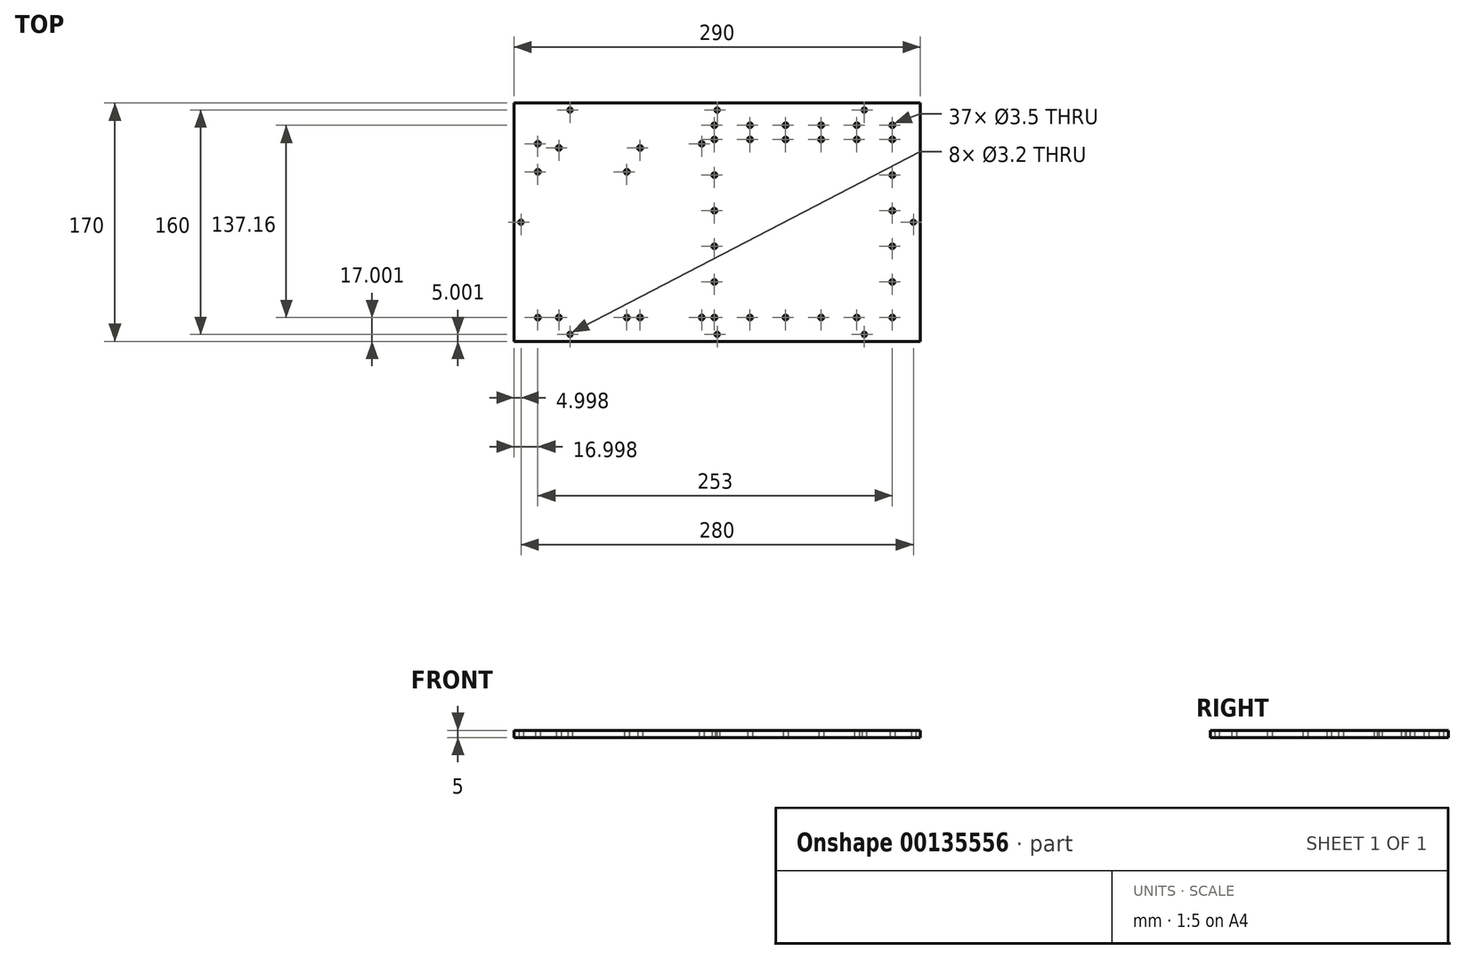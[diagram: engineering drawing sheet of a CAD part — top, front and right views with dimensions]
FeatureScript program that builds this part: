
annotation { "Feature Type Name" : "Feature", "Feature Type Description" : "" }
export const myFeature = defineFeature(function(context is Context, id is Id, definition is map)
    precondition{}
    {
        {
            var Q0;
            Q0=qCreatedBy(makeId("Top.planeOp"),FACE);
            var sketch = newSketch(context, id + "F0", { "sketchPlane" : qUnion([Q0])});
            skLineSegment(sketch, "E0", {"start": v(-144.23, 5.22) * mm, "end": v(155.77, 5.22) * mm, "construction": true});
            skLineSegment(sketch, "E1", {"start": v(5.77, 95.22) * mm, "end": v(5.77, -84.78) * mm, "construction": true});
            skLineSegment(sketch, "E2.bottom", {"start": v(-105.23, 90.22) * mm, "end": v(116.77, 90.22) * mm, "construction": true});
            skLineSegment(sketch, "E2.top", {"start": v(-139.23, -79.78) * mm, "end": v(150.77, -79.78) * mm, "construction": true});
            skLineSegment(sketch, "E2.left", {"start": v(-139.23, 65.22) * mm, "end": v(-139.23, -79.78) * mm, "construction": true});
            skLineSegment(sketch, "E2.right", {"start": v(150.77, 65.22) * mm, "end": v(150.77, -79.78) * mm, "construction": true});
            skLineSegment(sketch, "E3", {"start": v(-139.23, 90.22) * mm, "end": v(-105.23, 90.22) * mm});
            skLineSegment(sketch, "E4", {"start": v(-139.23, 90.22) * mm, "end": v(-139.23, 65.22) * mm});
            skLineSegment(sketch, "E5.MirrorCS", {"start": v(-139.23, -79.78) * mm, "end": v(-105.23, -79.78) * mm});
            skLineSegment(sketch, "E6.MirrorCS", {"start": v(-139.23, -79.78) * mm, "end": v(-139.23, -54.78) * mm});
            skLineSegment(sketch, "E7.MirrorCS", {"start": v(150.77, 90.22) * mm, "end": v(150.77, 65.22) * mm});
            skLineSegment(sketch, "E8.MirrorCS", {"start": v(150.77, 90.22) * mm, "end": v(116.77, 90.22) * mm});
            skLineSegment(sketch, "E9.MirrorCS", {"start": v(150.77, -79.78) * mm, "end": v(116.77, -79.78) * mm});
            skLineSegment(sketch, "E10.MirrorCS", {"start": v(150.77, -79.78) * mm, "end": v(150.77, -54.78) * mm});
            skLineSegment(sketch, "E11", {"start": v(-99.23, 112.7) * mm, "end": v(-99.23, -120.06) * mm, "construction": true});
            skLineSegment(sketch, "E12", {"start": v(110.77, 113.23) * mm, "end": v(110.77, -113.29) * mm, "construction": true});
            skLineSegment(sketch, "E13", {"start": v(-165.76, 85.22) * mm, "end": v(179.48, 85.22) * mm, "construction": true});
            skLineSegment(sketch, "E14", {"start": v(-160.04, -74.78) * mm, "end": v(189.9, -74.78) * mm, "construction": true});
            skLineSegment(sketch, "E15", {"start": v(145.77, 110.1) * mm, "end": v(145.77, -113.29) * mm, "construction": true});
            skLineSegment(sketch, "E16", {"start": v(-134.23, 116.87) * mm, "end": v(-134.23, -108.08) * mm, "construction": true});
            skCircle(sketch, "E17", {"center": v(5.77, 85.22) * mm, "radius": 1.6 * mm});
            skCircle(sketch, "E18", {"center": v(-99.23, 85.22) * mm, "radius": 1.6 * mm});
            skCircle(sketch, "E19", {"center": v(110.77, 85.22) * mm, "radius": 1.6 * mm});
            skCircle(sketch, "E20", {"center": v(145.77, 5.22) * mm, "radius": 1.6 * mm});
            skCircle(sketch, "E21", {"center": v(-134.23, 5.22) * mm, "radius": 1.6 * mm});
            skCircle(sketch, "E22", {"center": v(5.77, -74.78) * mm, "radius": 1.6 * mm});
            skCircle(sketch, "E23", {"center": v(110.77, -74.78) * mm, "radius": 1.6 * mm});
            skCircle(sketch, "E24", {"center": v(-99.23, -74.78) * mm, "radius": 1.6 * mm});
            skLineSegment(sketch, "E25", {"start": v(-105.23, 90.22) * mm, "end": v(116.77, 90.22) * mm});
            skLineSegment(sketch, "E26", {"start": v(116.77, -79.78) * mm, "end": v(-105.23, -79.78) * mm});
            skLineSegment(sketch, "E27", {"start": v(-139.23, -54.78) * mm, "end": v(-139.23, 65.22) * mm});
            skLineSegment(sketch, "E28", {"start": v(150.77, -54.78) * mm, "end": v(150.77, 65.22) * mm});
            skLineSegment(sketch, "E29", {"start": v(-122.23, 85.22) * mm, "end": v(-122.23, -74.78) * mm, "construction": true});
            skPoint(sketch, "E29.startSnap0", {"position": v(-122.23, 90.22) * mm});
            skLineSegment(sketch, "E30", {"start": v(130.77, 85.22) * mm, "end": v(130.77, -74.78) * mm, "construction": true});
            skLineSegment(sketch, "E31", {"start": v(-134.23, -62.78) * mm, "end": v(145.77, -62.78) * mm, "construction": true});
            skLineSegment(sketch, "E32", {"start": v(-5.23, 85.22) * mm, "end": v(-5.23, -62.78) * mm, "construction": true});
            skLineSegment(sketch, "E33", {"start": v(-5.23, 61.22) * mm, "end": v(-122.23, 61.22) * mm, "construction": true});
            skCircle(sketch, "E34", {"center": v(-122.23, 61.22) * mm, "radius": 1.75 * mm});
            skCircle(sketch, "E35", {"center": v(-122.23, -62.78) * mm, "radius": 1.75 * mm});
            skCircle(sketch, "E36", {"center": v(-5.23, -62.78) * mm, "radius": 1.75 * mm});
            skCircle(sketch, "E37", {"center": v(-5.23, 61.22) * mm, "radius": 1.75 * mm});
            skLineSegment(sketch, "E38", {"start": v(-122.23, 41.22) * mm, "end": v(-5.23, 41.22) * mm, "construction": true});
            skLineSegment(sketch, "E39", {"start": v(-58.73, 41.22) * mm, "end": v(-58.73, -62.78) * mm, "construction": true});
            skCircle(sketch, "E40", {"center": v(-122.23, 41.22) * mm, "radius": 1.75 * mm});
            skCircle(sketch, "E41", {"center": v(-58.73, 41.22) * mm, "radius": 1.75 * mm});
            skCircle(sketch, "E42", {"center": v(-58.73, -62.78) * mm, "radius": 1.75 * mm});
            skLineSegment(sketch, "E43", {"start": v(-107.23, -62.78) * mm, "end": v(-107.23, 61.22) * mm, "construction": true});
            skCircle(sketch, "E44", {"center": v(-107.23, -62.78) * mm, "radius": 1.75 * mm});
            skLineSegment(sketch, "E45", {"start": v(-49.23, 61.22) * mm, "end": v(-49.23, -62.78) * mm, "construction": true});
            skLineSegment(sketch, "E46", {"start": v(-107.23, 58.22) * mm, "end": v(-49.23, 58.22) * mm, "construction": true});
            skCircle(sketch, "E47", {"center": v(-107.23, 58.22) * mm, "radius": 1.75 * mm});
            skCircle(sketch, "E48", {"center": v(-49.23, 58.22) * mm, "radius": 1.75 * mm});
            skCircle(sketch, "E49", {"center": v(-49.23, -62.78) * mm, "radius": 1.75 * mm});
            skLineSegment(sketch, "E50", {"start": v(145.77, 74.38) * mm, "end": v(-134.23, 74.38) * mm, "construction": true});
            skLineSegment(sketch, "E51", {"start": v(3.77, 74.38) * mm, "end": v(3.77, -62.78) * mm, "construction": true});
            skCircle(sketch, "E52", {"center": v(130.77, -62.78) * mm, "radius": 1.75 * mm});
            skCircle(sketch, "E53.0.1.0", {"center": v(130.77, -37.38) * mm, "radius": 1.75 * mm});
            skCircle(sketch, "E53.0.2.0", {"center": v(130.77, -11.98) * mm, "radius": 1.75 * mm});
            skCircle(sketch, "E53.0.3.0", {"center": v(130.77, 13.42) * mm, "radius": 1.75 * mm});
            skCircle(sketch, "E53.0.4.0", {"center": v(130.77, 38.82) * mm, "radius": 1.75 * mm});
            skCircle(sketch, "E53.0.5.0", {"center": v(130.77, 64.22) * mm, "radius": 1.75 * mm});
            skLineSegment(sketch, "E53.direction1", {"start": v(130.77, -62.78) * mm, "end": v(155.77, -62.78) * mm, "construction": true});
            skLineSegment(sketch, "E53.direction2", {"start": v(130.77, -62.78) * mm, "end": v(130.77, -37.38) * mm, "construction": true});
            skCircle(sketch, "E54.1.0.0", {"center": v(105.37, -62.78) * mm, "radius": 1.75 * mm});
            skCircle(sketch, "E54.2.0.0", {"center": v(79.97, -62.78) * mm, "radius": 1.75 * mm});
            skCircle(sketch, "E54.3.0.0", {"center": v(54.57, -62.78) * mm, "radius": 1.75 * mm});
            skCircle(sketch, "E54.4.0.0", {"center": v(29.17, -62.78) * mm, "radius": 1.75 * mm});
            skCircle(sketch, "E54.5.0.0", {"center": v(3.77, -62.78) * mm, "radius": 1.75 * mm});
            skLineSegment(sketch, "E54.direction1", {"start": v(130.77, -62.78) * mm, "end": v(105.37, -62.78) * mm, "construction": true});
            skCircle(sketch, "E55.0.1.0", {"center": v(3.77, -37.38) * mm, "radius": 1.75 * mm});
            skCircle(sketch, "E55.0.2.0", {"center": v(3.77, -11.98) * mm, "radius": 1.75 * mm});
            skCircle(sketch, "E55.0.3.0", {"center": v(3.77, 13.42) * mm, "radius": 1.75 * mm});
            skCircle(sketch, "E55.0.4.0", {"center": v(3.77, 38.82) * mm, "radius": 1.75 * mm});
            skCircle(sketch, "E55.0.5.0", {"center": v(3.77, 64.22) * mm, "radius": 1.75 * mm});
            skLineSegment(sketch, "E55.direction1", {"start": v(3.77, -62.78) * mm, "end": v(28.77, -62.78) * mm, "construction": true});
            skLineSegment(sketch, "E55.direction2", {"start": v(3.77, -62.78) * mm, "end": v(3.77, -37.38) * mm, "construction": true});
            skLineSegment(sketch, "E56", {"start": v(3.77, 64.22) * mm, "end": v(130.77, 64.22) * mm, "construction": true});
            skCircle(sketch, "E57.1.0.0", {"center": v(105.37, 64.22) * mm, "radius": 1.75 * mm});
            skCircle(sketch, "E57.2.0.0", {"center": v(79.97, 64.22) * mm, "radius": 1.75 * mm});
            skCircle(sketch, "E57.3.0.0", {"center": v(54.57, 64.22) * mm, "radius": 1.75 * mm});
            skCircle(sketch, "E57.4.0.0", {"center": v(29.17, 64.22) * mm, "radius": 1.75 * mm});
            skLineSegment(sketch, "E57.direction1", {"start": v(130.77, 64.22) * mm, "end": v(105.37, 64.22) * mm, "construction": true});
            skCircle(sketch, "E58", {"center": v(130.77, 74.38) * mm, "radius": 1.75 * mm});
            skCircle(sketch, "E59.1.0.0", {"center": v(105.37, 74.38) * mm, "radius": 1.75 * mm});
            skCircle(sketch, "E59.2.0.0", {"center": v(79.97, 74.38) * mm, "radius": 1.75 * mm});
            skCircle(sketch, "E59.3.0.0", {"center": v(54.57, 74.38) * mm, "radius": 1.75 * mm});
            skCircle(sketch, "E59.4.0.0", {"center": v(29.17, 74.38) * mm, "radius": 1.75 * mm});
            skCircle(sketch, "E59.5.0.0", {"center": v(3.77, 74.38) * mm, "radius": 1.75 * mm});
            skLineSegment(sketch, "E59.direction1", {"start": v(130.77, 74.38) * mm, "end": v(105.37, 74.38) * mm, "construction": true});
            skSolve(sketch);
        }
        {
            var Q0;
            Q0 = qSketchRegion(id + "F0", true);
            extrude(context, id + "F1", {"entities" : qUnion([Q0]), "depth" : 5 * mm});
        }
    });
